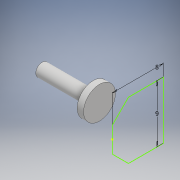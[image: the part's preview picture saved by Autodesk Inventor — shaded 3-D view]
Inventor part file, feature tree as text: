
AUTODESK INVENTOR PART (.ipt)
format: ipt  version: 2018 (Build 220112000, 112)  size: 187,392 bytes
history: native  units: mm
features: sketch x10, extrude x9, projected_geometry x1
ambient origin geometry x8: Origin, YZ Plane, XZ Plane, XY Plane, X Axis, Y Axis, Z Axis, Center Point
bodies: Solid1 (feature_tree)
feature tree (20):
  extrude  "Extrusion1"  Depth=10.0mm TaperAngle=0.0deg
  sketch  "Sketch2"  dims[d3=9.0mm d4=8.0mm d5=10.0mm d6=0.0mm]
  extrude  "Extrusion2"  Depth=10.0mm TaperAngle=0.0deg
  extrude  "Extrusion3"  Depth=1.125mm
  extrude  "Extrusion4"  Depth=1.6mm
  extrude  "Extrusion5"  Depth=1.8mm
  extrude  "Extrusion6"  Depth=2.4mm
  extrude  "Extrusion7"  Depth=3.32mm
  extrude  "Extrusion8"  Depth=10.0mm
  extrude  "Extrusion9"  Depth=15.0mm TaperAngle=0.0deg
  sketch  "Sketch1"  dims[d0=10.0mm d1=10.0mm d2=0.0mm]
  sketch  "Sketch3"  dims[d9=1.125mm d10=1.125mm]
  sketch  "Sketch4"  dims[d12=0.0mm d13=0.0mm d16=1.6mm]
  sketch  "Sketch5"  dims[d18=1.6mm d21=1.8mm]
  projected_geometry  "Projected Loop1"
  sketch  "Sketch6"  dims[d23=1.8mm d24=2.4mm]
  sketch  "Sketch7"  dims[d26=3.32mm d27=3.32mm]
  sketch  "Sketch8"  dims[d29=10.0mm d30=0.0mm d31=5.0mm]
  sketch  "Sketch9"  dims[d32=2.4mm d33=15.0mm d34=0.0mm]
  sketch  "Sketch10"  dims[d35=15.0mm d36=0.0mm d37=1.075mm d38=7.0mm d39=0.0mm d40=10.0mm d41=0.0mm d42=8.0mm d43=0.0mm]
